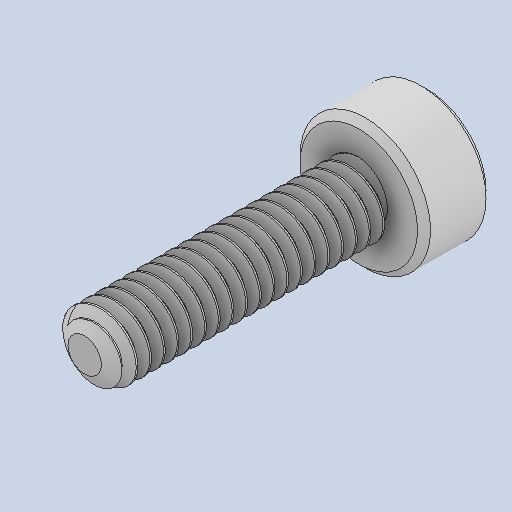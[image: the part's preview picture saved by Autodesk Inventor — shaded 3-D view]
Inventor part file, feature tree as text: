
AUTODESK INVENTOR PART (.ipt)
format: ipt  version: 2023 (Build 270158000, 158)  size: 699,392 bytes
history: native  units: mm
features: chamfer x1
ambient origin geometry x8: Origin, YZ Plane, XZ Plane, XY Plane, X Axis, Y Axis, Z Axis, Center Point
bodies: Solid1 (feature_tree)
feature tree (1):
  chamfer  "Chamfer1"  [1 undecoded]
note: 1 required parameter value undecoded (feature->parameter linkage not recoverable at this tier; creation-order binding heuristic only, values carry confidence <= 0.55)
